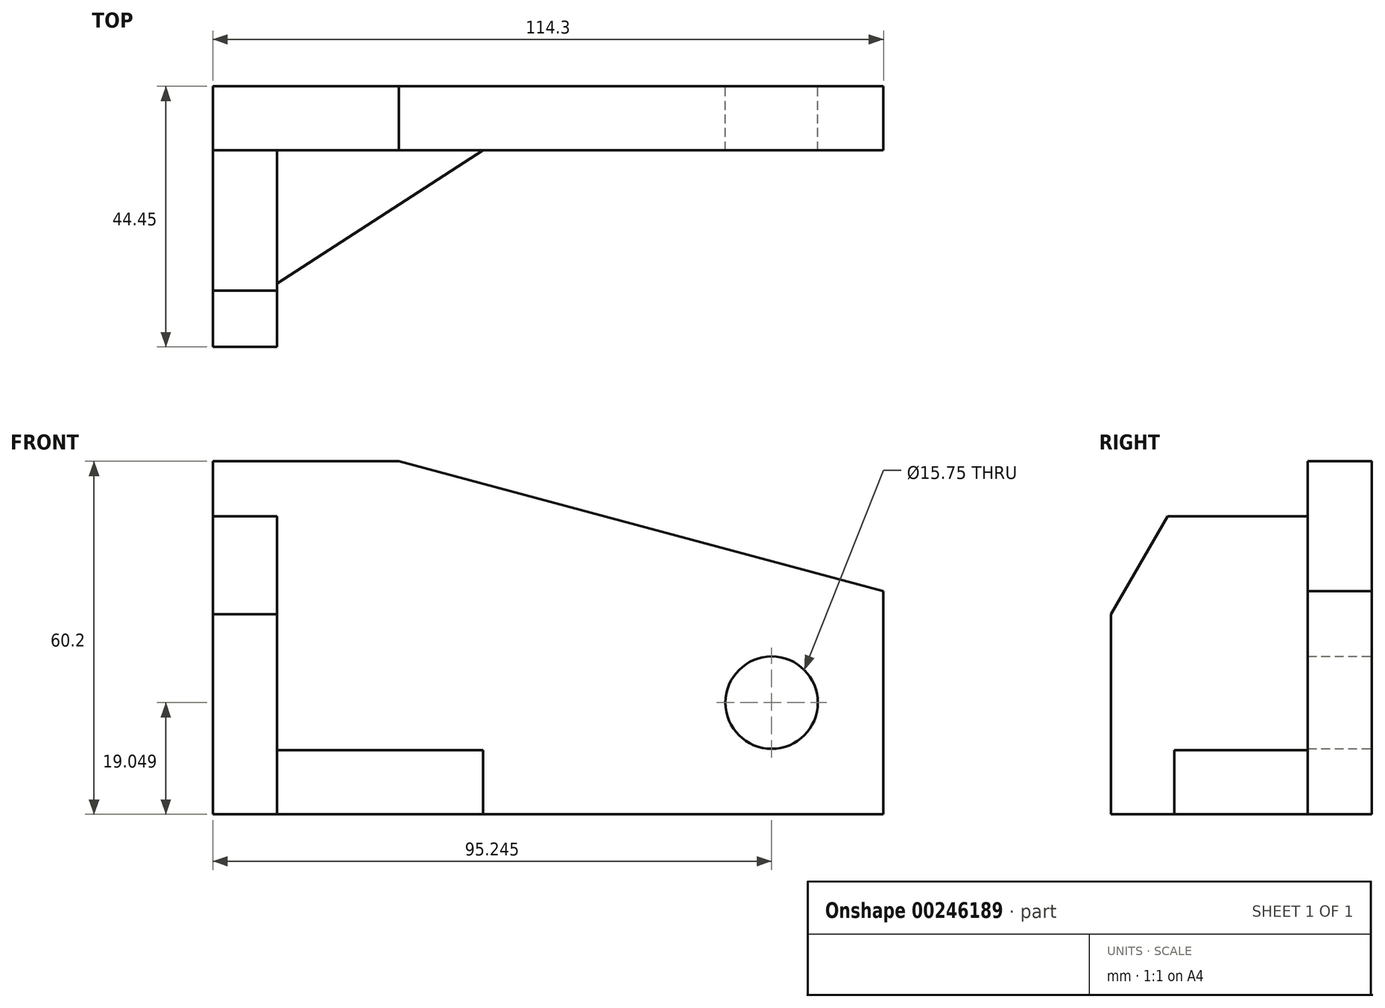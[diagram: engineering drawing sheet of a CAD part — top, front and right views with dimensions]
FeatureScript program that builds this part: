
annotation { "Feature Type Name" : "Feature", "Feature Type Description" : "" }
export const myFeature = defineFeature(function(context is Context, id is Id, definition is map)
    precondition{}
    {
        {
            var Q0;
            Q0=qCreatedBy(makeId("Front.planeOp"),FACE);
            var sketch = newSketch(context, id + "F0", { "sketchPlane" : qUnion([Q0])});
            skLineSegment(sketch, "E0.top", {"start": v(-60.77, -34.14) * mm, "end": v(-29.02, -34.14) * mm});
            skLineSegment(sketch, "E0.left", {"start": v(-60.77, 26.06) * mm, "end": v(-60.77, -34.14) * mm});
            skLineSegment(sketch, "E0.right", {"start": v(-29.02, 26.06) * mm, "end": v(-29.02, -34.14) * mm});
            skLineSegment(sketch, "E1.bottom", {"start": v(-60.77, 26.06) * mm, "end": v(-29.02, 26.06) * mm});
            skLineSegment(sketch, "E2.bottom", {"start": v(53.53, -34.14) * mm, "end": v(-29.02, -34.14) * mm});
            skLineSegment(sketch, "E2.top", {"start": v(53.53, 26.06) * mm, "end": v(-29.02, 26.06) * mm, "construction": true});
            skLineSegment(sketch, "E3", {"start": v(53.53, -34.14) * mm, "end": v(53.53, 3.94) * mm});
            skLineSegment(sketch, "E4", {"start": v(-29.02, 26.06) * mm, "end": v(53.53, 3.94) * mm});
            skLineSegment(sketch, "E5.top", {"start": v(53.53, -15.1) * mm, "end": v(34.48, -15.1) * mm, "construction": true});
            skCircle(sketch, "E6", {"center": v(34.48, -15.1) * mm, "radius": 7.87 * mm});
            skLineSegment(sketch, "E7", {"start": v(34.48, -15.1) * mm, "end": v(34.48, -34.14) * mm, "construction": true});
            skSolve(sketch);
        }
        {
            var Q0;
            Q0 = qSketchRegion(id + "F0", true);
            extrude(context, id + "F1", {"entities" : qUnion([Q0]), "depth" : 10.92 * mm});
        }
        {
            var Q0;
            Q0 = qSketchRegion(id + "F0", true);
            extrude(context, id + "F2", {"entities" : qUnion([Q0]), "operationType" : NewBodyOperationType.REMOVE, "oppositeDirection" : true, "depth" : 10.92 * mm});
        }
        {
            var Q0;
            Q0=makeQuery(id+"F1.opExtrude","CAP_FACE",FACE,{"disambiguationData":[OSD([sQuery(id+"F0.wireOp",EDGE,"E0.bottom"),sQuery(id+"F0.wireOp",EDGE,"E0.top"),sQuery(id+"F0.wireOp",EDGE,"E0.left"),sQuery(id+"F0.wireOp",EDGE,"E2.bottom"),sQuery(id+"F0.wireOp",EDGE,"E3"),sQuery(id+"F0.wireOp",EDGE,"E4"),sQuery(id+"F0.wireOp",EDGE,"E6")])],"isStart":false});
            var sketch = newSketch(context, id + "F3", { "sketchPlane" : qUnion([Q0])});
            skLineSegment(sketch, "E8.bottom", {"start": v(-60.77, 16.66) * mm, "end": v(-49.85, 16.66) * mm});
            skLineSegment(sketch, "E8.top", {"start": v(-60.77, -34.14) * mm, "end": v(-49.85, -34.14) * mm});
            skLineSegment(sketch, "E8.left", {"start": v(-60.77, 16.66) * mm, "end": v(-60.77, -34.14) * mm});
            skLineSegment(sketch, "E8.right", {"start": v(-49.85, 16.66) * mm, "end": v(-49.85, -34.14) * mm});
            skSolve(sketch);
        }
        {
            var Q0;
            Q0=makeQuery(id+"F3.imprint","IMPRINT",FACE,{"disambiguationData":[TD([[makeQuery(id+"F3.imprint","IMPRINT",EDGE,{"derivedFrom":sQuery(id+"F3.wireOp",EDGE,"E8.bottom")}),-1.0]])]});
            extrude(context, id + "F4", {"entities" : qUnion([Q0]), "operationType" : NewBodyOperationType.ADD, "depth" : 33.53 * mm});
        }
        {
            var Q0;
            Q0=makeQuery(id+"F4.boolean.opBoolean","MERGE",FACE,{"derivedFrom":[makeQuery(id+"F1.opExtrude","SWEPT_FACE",FACE,{"disambiguationData":[OSD([sQuery(id+"F0.wireOp",EDGE,"E0.left")])]}),makeQuery(id+"F4.opExtrude","SWEPT_FACE",FACE,{"disambiguationData":[OSD([sQuery(id+"F3.wireOp",EDGE,"E8.left")])]})]});
            var sketch = newSketch(context, id + "F5", { "sketchPlane" : qUnion([Q0])});
            skLineSegment(sketch, "E9", {"start": v(44.45, 0) * mm, "end": v(27.6, 29.18) * mm});
            skSolve(sketch);
        }
        {
            var Q0;
            {var subQ0=sQuery(id+"F5.wireOp",EDGE,"E9");var subQ1=sQuery(id+"F3.wireOp",EDGE,"E8.left");var subQ2=makeQuery(id+"F4.opExtrude","CAP_EDGE",EDGE,{"disambiguationData":[OSD([subQ1])],"isStart":false});var subQ3=makeQuery(id+"F5.imprint","INTERSECT",VERTEX,{"derivedFrom":[subQ2,subQ0]});Q0=makeQuery(id+"F5.imprint","IMPRINT",FACE,{"disambiguationData":[TD([[makeQuery(id+"F5.imprint","IMPRINT",EDGE,{"disambiguationData":[TD([[subQ3,-1.0]])],"derivedFrom":subQ0}),-1.0]])]});}
            extrude(context, id + "F6", {"entities" : qUnion([Q0]), "operationType" : NewBodyOperationType.REMOVE, "oppositeDirection" : true, "depth" : 10.92 * mm});
        }
        {
            var Q0;
            Q0=makeQuery(id+"F4.opExtrude","SWEPT_FACE",FACE,{"disambiguationData":[OSD([sQuery(id+"F3.wireOp",EDGE,"E8.right")])]});
            var sketch = newSketch(context, id + "F7", { "sketchPlane" : qUnion([Q0])});
            skLineSegment(sketch, "E10.bottom", {"start": v(-10.92, -34.14) * mm, "end": v(-44.45, -34.14) * mm});
            skLineSegment(sketch, "E10.top", {"start": v(-10.92, -23.22) * mm, "end": v(-44.45, -23.22) * mm});
            skLineSegment(sketch, "E10.left", {"start": v(-10.92, -34.14) * mm, "end": v(-10.92, -23.22) * mm});
            skLineSegment(sketch, "E10.right", {"start": v(-44.45, -34.14) * mm, "end": v(-44.45, -23.22) * mm});
            skSolve(sketch);
        }
        {
            var Q0;
            Q0 = qSketchRegion(id + "F7", true);
            extrude(context, id + "F8", {"entities" : qUnion([Q0]), "operationType" : NewBodyOperationType.ADD, "depth" : 52.58 * mm});
        }
        {
            var Q0;
            Q0=makeQuery(id+"F8.opExtrude","SWEPT_FACE",FACE,{"disambiguationData":[OSD([sQuery(id+"F7.wireOp",EDGE,"E10.top")])]});
            var sketch = newSketch(context, id + "F9", { "sketchPlane" : qUnion([Q0])});
            skLineSegment(sketch, "E11", {"start": v(-66.58, -44.45) * mm, "end": v(-14.7, -10.92) * mm});
            skSolve(sketch);
        }
        {
            var Q0;
            Q0 = qSketchRegion(id + "F9", true);
            var Q1;
            {var subQ0=sQuery(id+"F9.wireOp",EDGE,"E11");Q1=makeQuery(id+"F9.imprint","IMPRINT",FACE,{"disambiguationData":[TD([[makeQuery(id+"F9.imprint","IMPRINT",EDGE,{"derivedFrom":subQ0}),-1.0]])]});}
            extrude(context, id + "F10", {"entities" : qUnion([Q0, Q1]), "operationType" : NewBodyOperationType.REMOVE, "oppositeDirection" : true, "depth" : 10.92 * mm});
        }
    });
